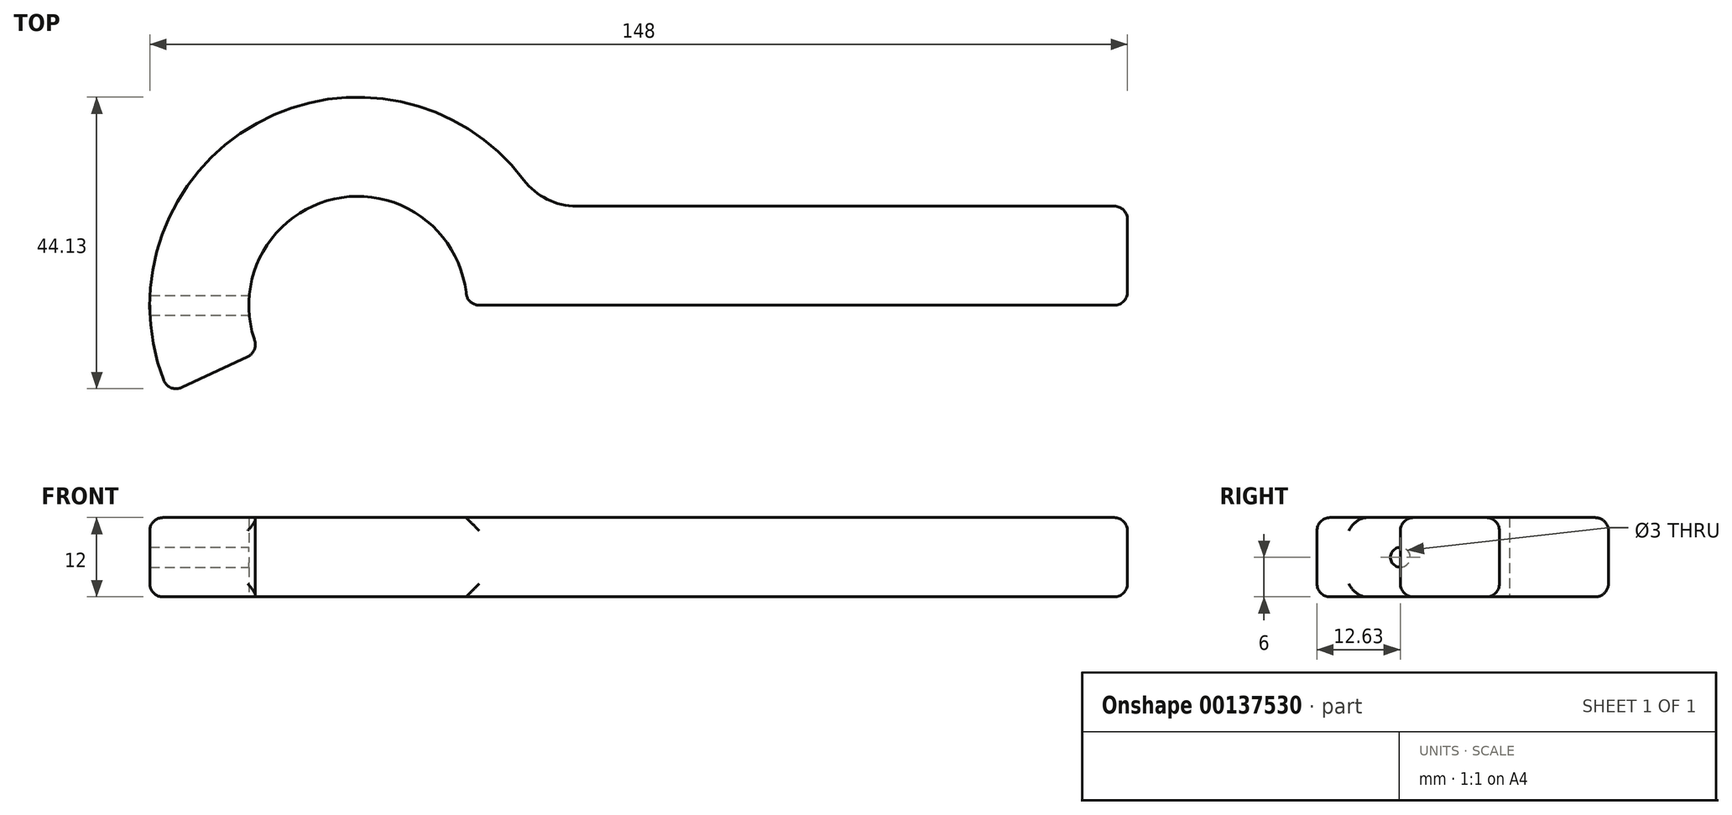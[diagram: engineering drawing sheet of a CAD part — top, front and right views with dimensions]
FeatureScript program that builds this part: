
annotation { "Feature Type Name" : "Feature", "Feature Type Description" : "" }
export const myFeature = defineFeature(function(context is Context, id is Id, definition is map)
    precondition{}
    {
        {
            var Q0;
            Q0=qCreatedBy(makeId("Top.planeOp"),FACE);
            var sketch = newSketch(context, id + "F0", { "sketchPlane" : qUnion([Q0])});
            skArc(sketch, "E0", {"start": v(16.5, 0) * mm, "mid": v(-3.57, 16.1) * mm, "end": v(-14.95, -6.97) * mm});
            skArc(sketch, "E1.0", {"start": v(27.7, 15) * mm, "mid": v(-14.16, 28.14) * mm, "end": v(-28.55, -13.31) * mm});
            skLineSegment(sketch, "E2", {"start": v(16.5, 0) * mm, "end": v(116.5, 0) * mm});
            skLineSegment(sketch, "E3", {"start": v(116.5, 0) * mm, "end": v(116.5, 15) * mm});
            skLineSegment(sketch, "E4", {"start": v(116.5, 15) * mm, "end": v(27.7, 15) * mm});
            skLineSegment(sketch, "E5", {"start": v(-14.95, -6.97) * mm, "end": v(-28.55, -13.31) * mm});
            skSolve(sketch);
        }
        {
            var Q0;
            Q0 = qSketchRegion(id + "F0", true);
            extrude(context, id + "F1", {"entities" : qUnion([Q0]), "depth" : 12 * mm});
        }
        {
            var Q0;
            Q0=qCreatedBy(makeId("Right.planeOp"),FACE);
            var sketch = newSketch(context, id + "F2", { "sketchPlane" : qUnion([Q0])});
            skCircle(sketch, "E6", {"center": v(0, 6) * mm, "radius": 1.5 * mm});
            skLineSegment(sketch, "E7.0", {"start": v(-13.31, 12) * mm, "end": v(-13.31, 0) * mm, "construction": true});
            skPoint(sketch, "E8", {"position": v(-13.31, 6) * mm});
            skSolve(sketch);
        }
        {
            var Q0;
            Q0 = qSketchRegion(id + "F2", true);
            extrude(context, id + "F3", {"entities" : qUnion([Q0]), "operationType" : NewBodyOperationType.REMOVE, "oppositeDirection" : true, "depth" : 50 * mm});
        }
        {
            var Q0;
            Q0=makeQuery(id+"F1.opExtrude","SWEPT_EDGE",EDGE,{"disambiguationData":[OSD([sQuery(id+"F0.wireOp",EDGE,"E1.0"),sQuery(id+"F0.wireOp",EDGE,"E4")])]});
            fillet(context, id + "F4", {"entities" : qUnion([Q0]), "radius" : 10 * mm, "tangentPropagation" : true, "allowEdgeOverflow" : false});
        }
        {
            var Q0;
            Q0=makeQuery(id+"F1.opExtrude","CAP_EDGE",EDGE,{"disambiguationData":[OSD([sQuery(id+"F0.wireOp",EDGE,"E1.0")])],"isStart":false});
            var Q1;
            Q1=makeQuery(id+"F1.opExtrude","CAP_EDGE",EDGE,{"disambiguationData":[OSD([sQuery(id+"F0.wireOp",EDGE,"E4")])],"isStart":false});
            var Q2;
            Q2=makeQuery(id+"F1.opExtrude","CAP_EDGE",EDGE,{"disambiguationData":[OSD([sQuery(id+"F0.wireOp",EDGE,"E2")])],"isStart":false});
            var Q3;
            Q3=makeQuery(id+"F1.opExtrude","CAP_EDGE",EDGE,{"disambiguationData":[OSD([sQuery(id+"F0.wireOp",EDGE,"E3")])],"isStart":false});
            var Q4;
            Q4=makeQuery(id+"F1.opExtrude","CAP_EDGE",EDGE,{"disambiguationData":[OSD([sQuery(id+"F0.wireOp",EDGE,"E2")])],"isStart":true});
            var Q5;
            Q5=makeQuery(id+"F1.opExtrude","SWEPT_EDGE",EDGE,{"disambiguationData":[OSD([sQuery(id+"F0.wireOp",EDGE,"E2"),sQuery(id+"F0.wireOp",EDGE,"E3")])]});
            var Q6;
            Q6=makeQuery(id+"F1.opExtrude","CAP_EDGE",EDGE,{"disambiguationData":[OSD([sQuery(id+"F0.wireOp",EDGE,"E1.0")])],"isStart":true});
            var Q7;
            Q7=makeQuery(id+"F1.opExtrude","SWEPT_EDGE",EDGE,{"disambiguationData":[OSD([sQuery(id+"F0.wireOp",EDGE,"E1.0"),sQuery(id+"F0.wireOp",EDGE,"E5")])]});
            var Q8;
            Q8=makeQuery(id+"F1.opExtrude","CAP_EDGE",EDGE,{"disambiguationData":[OSD([sQuery(id+"F0.wireOp",EDGE,"E4")])],"isStart":true});
            var Q9;
            Q9=makeQuery(id+"F1.opExtrude","CAP_EDGE",EDGE,{"disambiguationData":[OSD([sQuery(id+"F0.wireOp",EDGE,"E3")])],"isStart":true});
            var Q10;
            Q10=makeQuery(id+"F1.opExtrude","SWEPT_EDGE",EDGE,{"disambiguationData":[OSD([sQuery(id+"F0.wireOp",EDGE,"E3"),sQuery(id+"F0.wireOp",EDGE,"E4")])]});
            var Q11;
            Q11=makeQuery(id+"F1.opExtrude","CAP_EDGE",EDGE,{"disambiguationData":[OSD([sQuery(id+"F0.wireOp",EDGE,"E5")])],"isStart":true});
            var Q12;
            Q12=makeQuery(id+"F1.opExtrude","CAP_EDGE",EDGE,{"disambiguationData":[OSD([sQuery(id+"F0.wireOp",EDGE,"E5")])],"isStart":false});
            var Q13;
            Q13=makeQuery(id+"F1.opExtrude","SWEPT_EDGE",EDGE,{"disambiguationData":[OSD([sQuery(id+"F0.wireOp",EDGE,"E0"),sQuery(id+"F0.wireOp",EDGE,"E5")])]});
            var Q14;
            Q14=makeQuery(id+"F1.opExtrude","SWEPT_EDGE",EDGE,{"disambiguationData":[OSD([sQuery(id+"F0.wireOp",EDGE,"E0"),sQuery(id+"F0.wireOp",EDGE,"E2")])]});
            fillet(context, id + "F5", {"entities" : qUnion([Q0, Q1, Q2, Q3, Q4, Q5, Q6, Q7, Q8, Q9, Q10, Q11, Q12, Q13, Q14]), "radius" : 2 * mm, "tangentPropagation" : true, "allowEdgeOverflow" : false});
        }
    });
